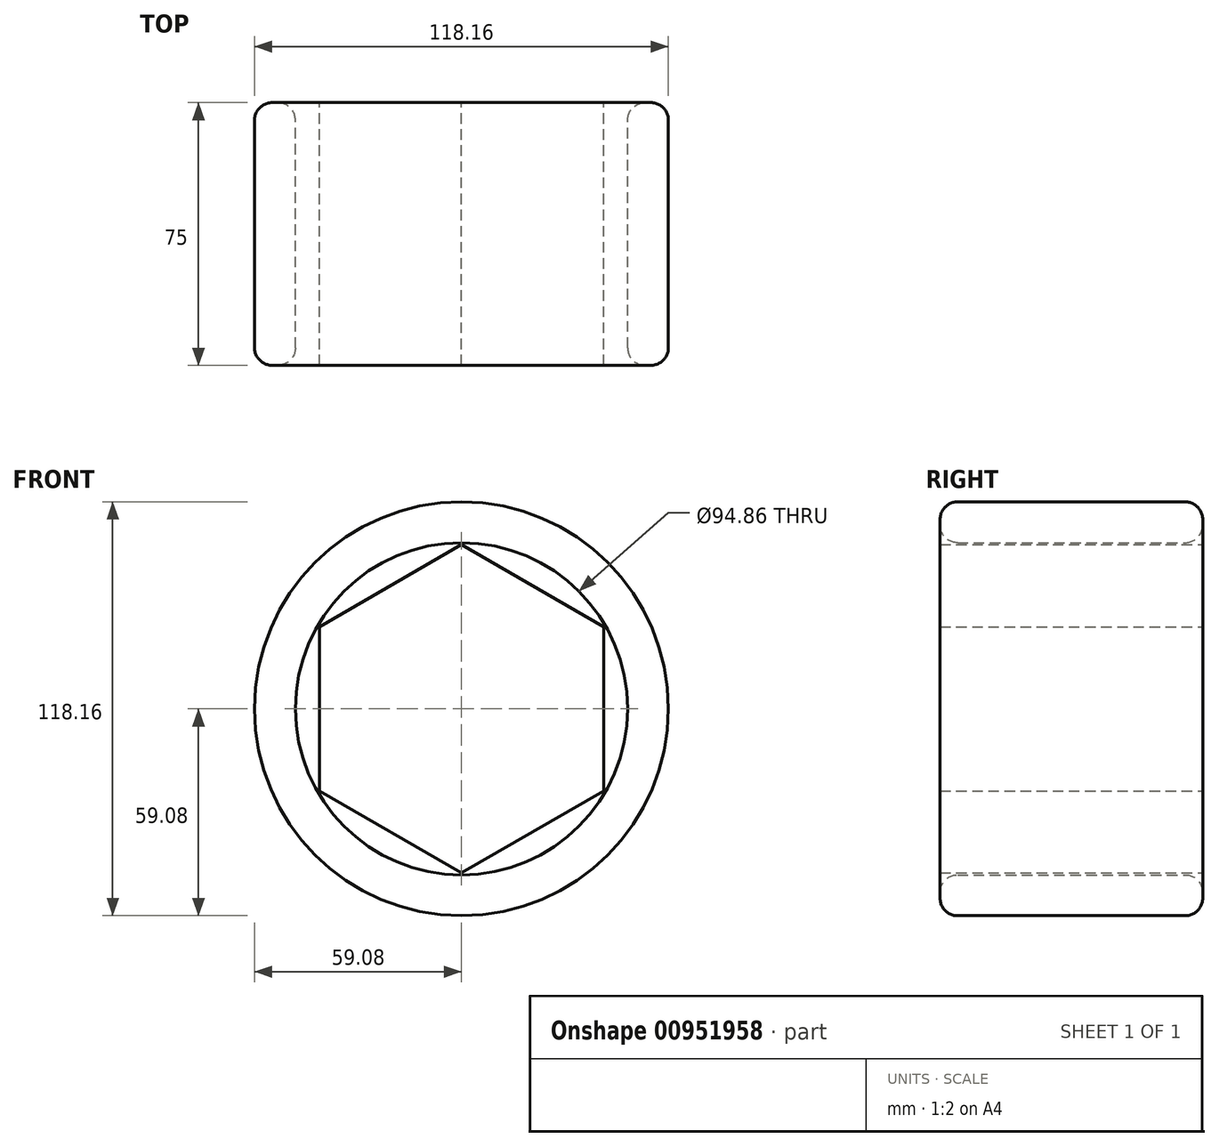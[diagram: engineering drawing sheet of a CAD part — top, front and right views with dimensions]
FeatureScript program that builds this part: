
annotation { "Feature Type Name" : "Feature", "Feature Type Description" : "" }
export const myFeature = defineFeature(function(context is Context, id is Id, definition is map)
    precondition{}
    {
        {
            var Q0;
            Q0=qCreatedBy(makeId("Front.planeOp"),FACE);
            var sketch = newSketch(context, id + "F0", { "sketchPlane" : qUnion([Q0])});
            skCircle(sketch, "E0", {"center": v(0, 0) * mm, "radius": 47.43 * mm});
            skCircle(sketch, "E1", {"center": v(0, 0) * mm, "radius": 59.08 * mm});
            skSolve(sketch);
        }
        {
            var Q0;
            Q0=makeQuery(id+"F0.imprint","IMPRINT",FACE,{"disambiguationData":[TD([[makeQuery(id+"F0.imprint","IMPRINT",EDGE,{"derivedFrom":sQuery(id+"F0.wireOp",EDGE,"E0")}),-1.0]])]});
            extrude(context, id + "F1", {"entities" : qUnion([Q0]), "depth" : 75 * mm, "offsetDistance" : 25 * mm});
        }
        {
            var Q0;
            Q0=makeQuery(id+"F1.opExtrude","CAP_EDGE",EDGE,{"disambiguationData":[OSD([sQuery(id+"F0.wireOp",EDGE,"E1")])],"isStart":false});
            var Q1;
            Q1=makeQuery(id+"F1.opExtrude","CAP_EDGE",EDGE,{"disambiguationData":[OSD([sQuery(id+"F0.wireOp",EDGE,"E0")])],"isStart":false});
            var Q2;
            Q2=makeQuery(id+"F1.opExtrude","CAP_FACE",FACE,{"disambiguationData":[OSD([sQuery(id+"F0.wireOp",EDGE,"E0"),sQuery(id+"F0.wireOp",EDGE,"E1")])],"isStart":true});
            fillet(context, id + "F2", {"entities" : qUnion([Q0, Q1, Q2]), "radius" : 5 * mm, "tangentPropagation" : true, "allowEdgeOverflow" : false});
        }
        {
            var Q0;
            Q0=qCreatedBy(makeId("Front.planeOp"),FACE);
            var sketch = newSketch(context, id + "F3", { "sketchPlane" : qUnion([Q0])});
            skCircle(sketch, "E2.cCircle", {"center": v(0, 0) * mm, "radius": 40.59 * mm, "construction": true});
            skLineSegment(sketch, "E2.0", {"start": v(40.59, 23.43) * mm, "end": v(40.59, -23.43) * mm});
            skLineSegment(sketch, "E2.1", {"start": v(40.59, -23.43) * mm, "end": v(0, -46.87) * mm});
            skLineSegment(sketch, "E2.2", {"start": v(0, -46.87) * mm, "end": v(-40.59, -23.43) * mm});
            skLineSegment(sketch, "E2.3", {"start": v(-40.59, -23.43) * mm, "end": v(-40.59, 23.43) * mm});
            skLineSegment(sketch, "E2.4", {"start": v(-40.59, 23.43) * mm, "end": v(0, 46.87) * mm});
            skLineSegment(sketch, "E2.5", {"start": v(0, 46.87) * mm, "end": v(40.59, 23.43) * mm});
            skPoint(sketch, "E2.0.midPoint", {"position": v(40.59, 0) * mm});
            skSolve(sketch);
        }
        {
            var Q0;
            Q0=qCreatedBy(makeId("Front.planeOp"),FACE);
            var sketch = newSketch(context, id + "F4", { "sketchPlane" : qUnion([Q0])});
            skLineSegment(sketch, "E3", {"start": v(-40.15, 23.04) * mm, "end": v(39.27, -22.6) * mm});
            skLineSegment(sketch, "E4", {"start": v(39.27, -22.6) * mm, "end": v(39.27, 23.91) * mm});
            skLineSegment(sketch, "E5", {"start": v(39.27, 23.91) * mm, "end": v(-39.27, -22.6) * mm});
            skLineSegment(sketch, "E6", {"start": v(-39.27, -22.6) * mm, "end": v(-40.15, 23.04) * mm});
            skSolve(sketch);
        }
        {
            var Q0;
            Q0 = qSketchRegion(id + "F4", true);
            var Q1;
            Q1=makeQuery(id+"F3.imprint","IMPRINT",FACE,{"disambiguationData":[TD([[makeQuery(id+"F3.imprint","IMPRINT",EDGE,{"derivedFrom":sQuery(id+"F3.wireOp",EDGE,"E2.0")}),-1.0]])]});
            extrude(context, id + "F5", {"entities" : qUnion([Q0, Q1]), "depth" : 75 * mm, "offsetDistance" : 25 * mm});
        }
        {
            var Q0;
            Q0=makeQuery(id+"F5.opExtrude","SWEPT_BODY",BODY,{"disambiguationData":[OSD([sQuery(id+"F4.wireOp",EDGE,"E3"),sQuery(id+"F4.wireOp",EDGE,"E5"),sQuery(id+"F4.wireOp",EDGE,"E6")])]});
            var Q1;
            Q1=makeQuery(id+"F5.opExtrude","SWEPT_BODY",BODY,{"disambiguationData":[OSD([sQuery(id+"F4.wireOp",EDGE,"E3"),sQuery(id+"F4.wireOp",EDGE,"E4"),sQuery(id+"F4.wireOp",EDGE,"E5")])]});
            deleteBodies(context, id + "F6", {"entities" : qUnion([Q0, Q1])});
        }
    });
